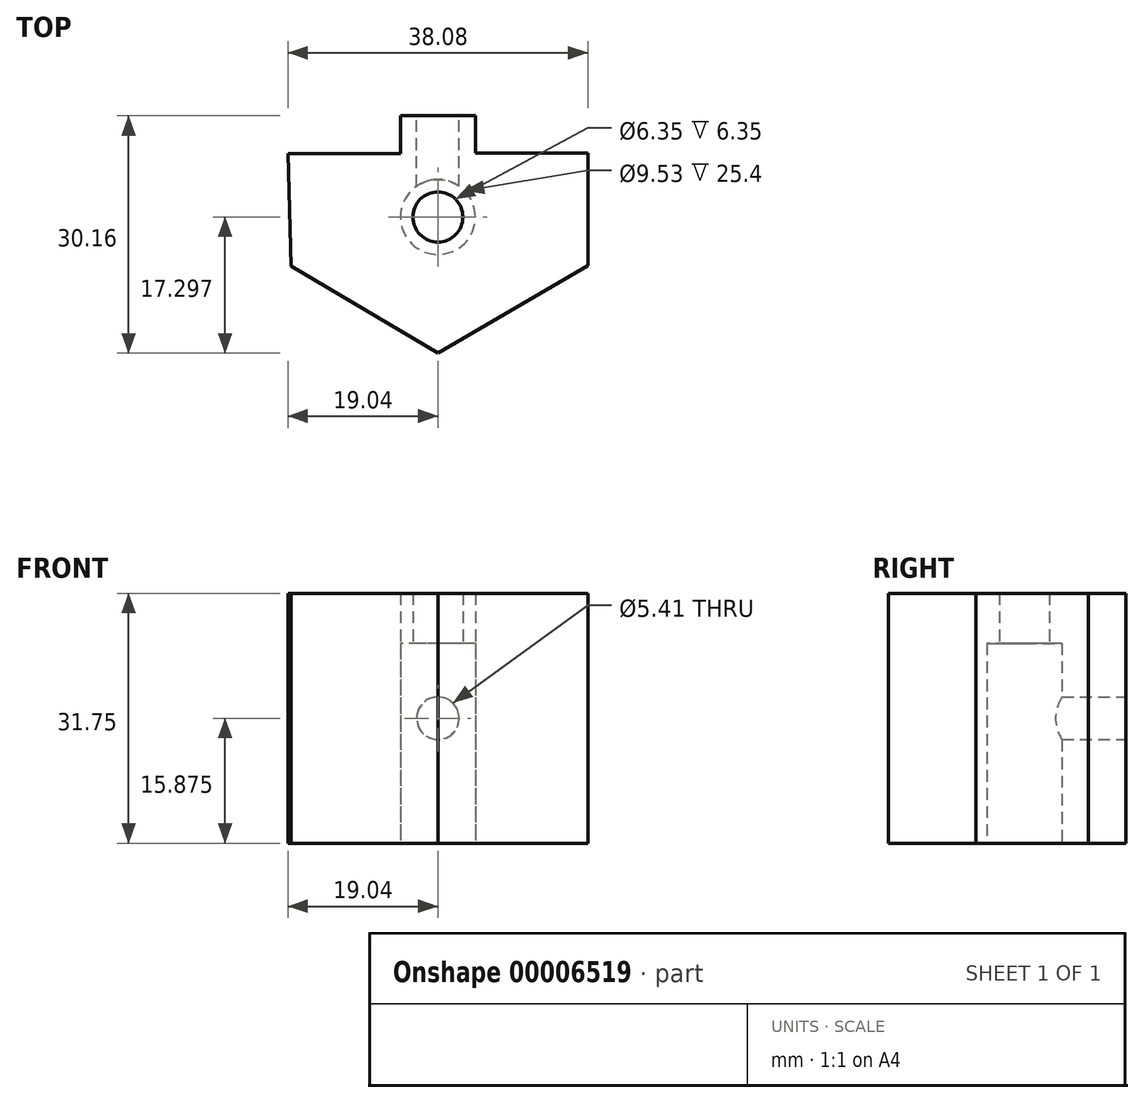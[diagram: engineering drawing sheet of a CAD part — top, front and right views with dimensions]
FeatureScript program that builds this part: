
annotation { "Feature Type Name" : "Feature", "Feature Type Description" : "" }
export const myFeature = defineFeature(function(context is Context, id is Id, definition is map)
    precondition{}
    {
        {
            var Q0;
            Q0=qCreatedBy(makeId("Top.planeOp"),FACE);
            var sketch = newSketch(context, id + "F0", { "sketchPlane" : qUnion([Q0])});
            skLineSegment(sketch, "E0", {"start": v(-19.04, 12.62) * mm, "end": v(-4.75, 12.62) * mm});
            skLineSegment(sketch, "E1", {"start": v(-4.75, 12.62) * mm, "end": v(-4.75, 17.4) * mm});
            skLineSegment(sketch, "E2", {"start": v(-4.75, 17.4) * mm, "end": v(4.75, 17.4) * mm});
            skLineSegment(sketch, "E3", {"start": v(4.75, 17.4) * mm, "end": v(4.75, 12.64) * mm});
            skLineSegment(sketch, "E4", {"start": v(4.75, 12.64) * mm, "end": v(19.04, 12.64) * mm});
            skLineSegment(sketch, "E5", {"start": v(19.04, 12.64) * mm, "end": v(19.04, -1.65) * mm});
            skLineSegment(sketch, "E6", {"start": v(19.04, -1.65) * mm, "end": v(0, -12.76) * mm});
            skLineSegment(sketch, "E7", {"start": v(0, -12.76) * mm, "end": v(-18.65, -1.66) * mm});
            skLineSegment(sketch, "E8", {"start": v(-18.65, -1.66) * mm, "end": v(-19.04, 12.62) * mm});
            skLineSegment(sketch, "E9", {"start": v(0, 34.8) * mm, "end": v(0, -44.4) * mm, "construction": true});
            skPoint(sketch, "E10", {"position": v(0, 17.4) * mm});
            skCircle(sketch, "E11", {"center": v(0, 4.54) * mm, "radius": 3.18 * mm});
            skCircle(sketch, "E12", {"center": v(0, 4.54) * mm, "radius": 4.76 * mm});
            skSolve(sketch);
        }
        {
            var Q0;
            Q0=makeQuery(id+"F0.imprint","IMPRINT",FACE,{"disambiguationData":[TD([[makeQuery(id+"F0.imprint","IMPRINT",EDGE,{"derivedFrom":sQuery(id+"F0.wireOp",EDGE,"E0")}),-1.0]])]});
            var Q1;
            Q1=makeQuery(id+"F0.imprint","IMPRINT",FACE,{"disambiguationData":[TD([[makeQuery(id+"F0.imprint","IMPRINT",EDGE,{"derivedFrom":sQuery(id+"F0.wireOp",EDGE,"E11")}),-1.0]])]});
            extrude(context, id + "F1", {"entities" : qUnion([Q0, Q1]), "depth" : 31.75 * mm});
        }
        {
            var Q0;
            Q0=makeQuery(id+"F0.imprint","IMPRINT",FACE,{"disambiguationData":[TD([[makeQuery(id+"F0.imprint","IMPRINT",EDGE,{"derivedFrom":sQuery(id+"F0.wireOp",EDGE,"E11")}),-1.0]])]});
            extrude(context, id + "F2", {"entities" : qUnion([Q0]), "operationType" : NewBodyOperationType.REMOVE, "depth" : 25.4 * mm});
        }
        {
            var Q0;
            Q0=makeQuery(id+"F1.opExtrude","SWEPT_FACE",FACE,{"disambiguationData":[OSD([sQuery(id+"F0.wireOp",EDGE,"E2")])]});
            var sketch = newSketch(context, id + "F3", { "sketchPlane" : qUnion([Q0])});
            skLineSegment(sketch, "E13", {"start": v(0, 52.13) * mm, "end": v(0, -9.1) * mm, "construction": true});
            skCircle(sketch, "E14", {"center": v(0, 15.88) * mm, "radius": 2.7 * mm});
            skSolve(sketch);
        }
        {
            var Q0;
            Q0=makeQuery(id+"F3.imprint","IMPRINT",FACE,{"disambiguationData":[TD([[makeQuery(id+"F3.imprint","IMPRINT",EDGE,{"derivedFrom":sQuery(id+"F3.wireOp",EDGE,"E14")}),1.0]])]});
            extrude(context, id + "F4", {"entities" : qUnion([Q0]), "operationType" : NewBodyOperationType.REMOVE, "oppositeDirection" : true, "depth" : 12.28 * mm});
        }
    });
